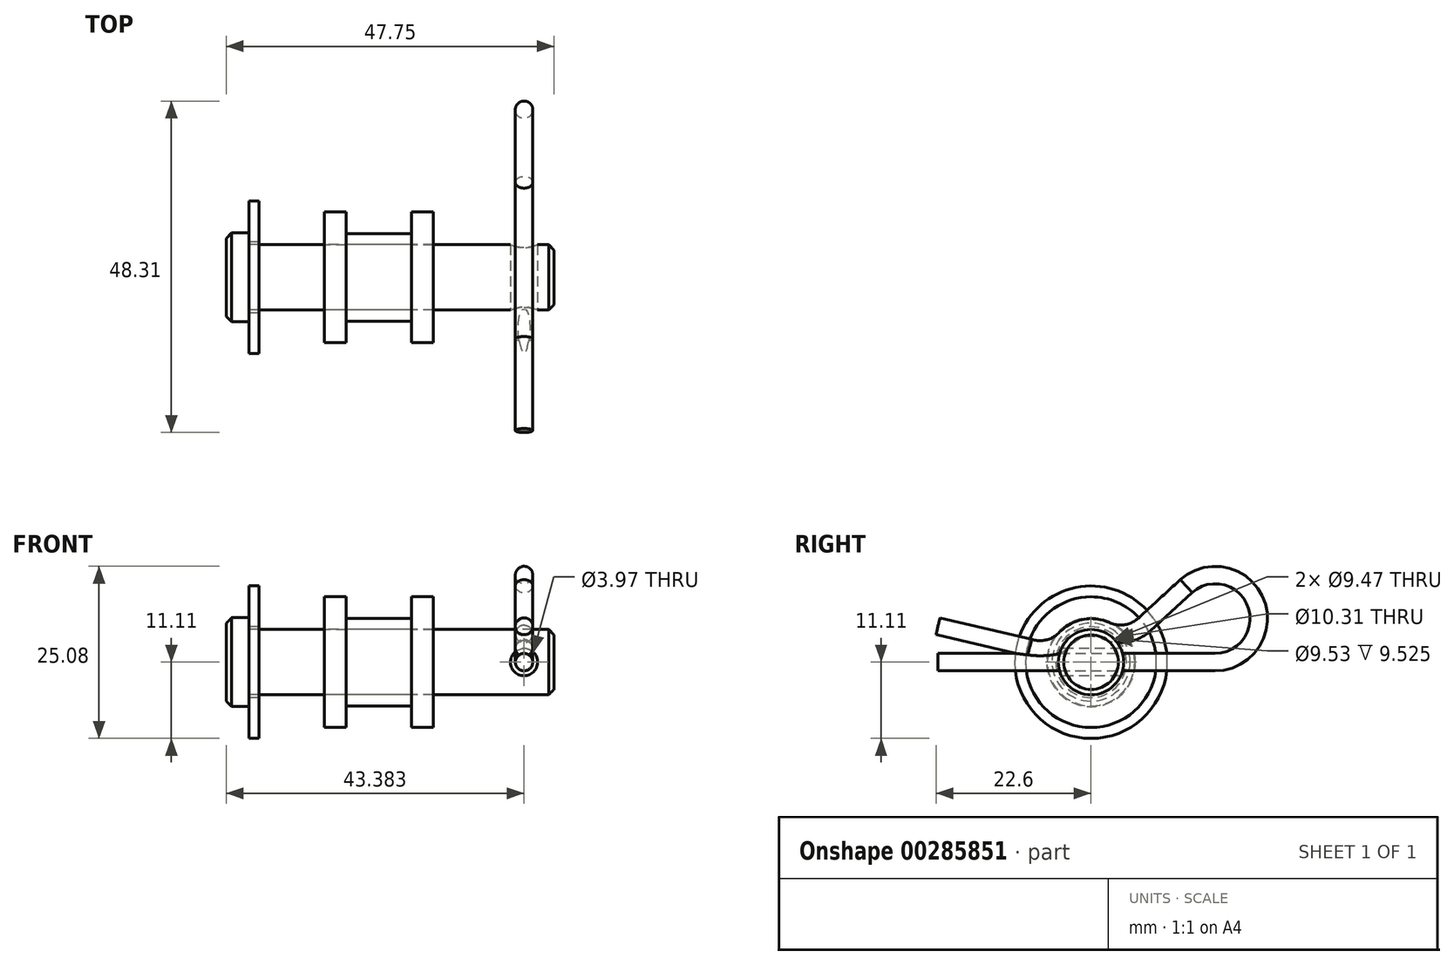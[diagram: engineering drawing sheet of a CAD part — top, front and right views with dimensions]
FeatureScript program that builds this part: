
annotation { "Feature Type Name" : "Feature", "Feature Type Description" : "" }
export const myFeature = defineFeature(function(context is Context, id is Id, definition is map)
    precondition{}
    {
        {
            var Q0;
            Q0=qCreatedBy(makeId("Front.planeOp"),FACE);
            var sketch = newSketch(context, id + "F0", { "sketchPlane" : qUnion([Q0])});
            skLineSegment(sketch, "E0", {"start": v(0, 0) * mm, "end": v(47.75, 0) * mm, "construction": true});
            skLineSegment(sketch, "E1", {"start": v(0, 0) * mm, "end": v(0, 6.48) * mm});
            skLineSegment(sketch, "E2", {"start": v(0, 6.48) * mm, "end": v(3.3, 6.48) * mm});
            skLineSegment(sketch, "E3", {"start": v(3.3, 6.48) * mm, "end": v(3.3, 4.76) * mm});
            skLineSegment(sketch, "E4", {"start": v(3.3, 4.76) * mm, "end": v(47.75, 4.76) * mm});
            skLineSegment(sketch, "E5", {"start": v(47.75, 4.76) * mm, "end": v(47.75, 0) * mm});
            skLineSegment(sketch, "E6", {"start": v(0, 0) * mm, "end": v(47.75, 0) * mm});
            skCircle(sketch, "E7", {"center": v(43.38, 0) * mm, "radius": 1.98 * mm});
            skSolve(sketch);
        }
        {
            var Q0;
            {var subQ0=sQuery(id+"F0.wireOp",EDGE,"E1");Q0=makeQuery(id+"F0.imprint","IMPRINT",FACE,{"disambiguationData":[TD([[makeQuery(id+"F0.imprint","IMPRINT",EDGE,{"derivedFrom":subQ0}),-1.0]])]});}
            var Q1;
            {var subQ0=sQuery(id+"F0.wireOp",EDGE,"E7");var subQ1=sQuery(id+"F0.wireOp",EDGE,"E6");var subQ2=makeQuery(id+"F0.imprint","INTERSECT",VERTEX,{"disambiguationData":[OD(0.0)],"derivedFrom":[subQ1,subQ0]});Q1=makeQuery(id+"F0.imprint","IMPRINT",FACE,{"disambiguationData":[TD([[makeQuery(id+"F0.imprint","IMPRINT",EDGE,{"disambiguationData":[TD([[subQ2,-1.0]])],"derivedFrom":subQ1}),1.0]])]});}
            var Q2;
            Q2=sQuery(id+"F0.wireOp",EDGE,"E6");
            revolve(context, id + "F1", {"entities" : qUnion([Q0, Q1]), "axis" : qUnion([Q2]), "revolveType" : RevolveType.FULL});
        }
        {
            var Q0;
            {var subQ0=sQuery(id+"F0.wireOp",EDGE,"E7");var subQ1=sQuery(id+"F0.wireOp",EDGE,"E6");var subQ2=makeQuery(id+"F0.imprint","INTERSECT",VERTEX,{"disambiguationData":[OD(0.0)],"derivedFrom":[subQ1,subQ0]});Q0=makeQuery(id+"F0.imprint","IMPRINT",FACE,{"disambiguationData":[TD([[makeQuery(id+"F0.imprint","IMPRINT",EDGE,{"disambiguationData":[TD([[subQ2,-1.0]])],"derivedFrom":subQ1}),-1.0]])]});}
            var Q1;
            {var subQ0=sQuery(id+"F0.wireOp",EDGE,"E7");var subQ1=sQuery(id+"F0.wireOp",EDGE,"E6");var subQ2=makeQuery(id+"F0.imprint","INTERSECT",VERTEX,{"disambiguationData":[OD(0.0)],"derivedFrom":[subQ1,subQ0]});Q1=makeQuery(id+"F0.imprint","IMPRINT",FACE,{"disambiguationData":[TD([[makeQuery(id+"F0.imprint","IMPRINT",EDGE,{"disambiguationData":[TD([[subQ2,-1.0]])],"derivedFrom":subQ1}),1.0]])]});}
            extrude(context, id + "F2", {"entities" : qUnion([Q0, Q1]), "operationType" : NewBodyOperationType.REMOVE, "endBound" : BoundingType.THROUGH_ALL, "oppositeDirection" : true, "depth" : 25.4 * mm, "hasSecondDirection" : true, "secondDirectionBound" : SecondDirectionBoundingType.THROUGH_ALL, "secondDirectionOppositeDirection" : false, "secondDirectionDepth" : 25.4 * mm});
        }
        {
            var Q0;
            Q0=makeQuery(id+"F1.opRevolve","SWEPT_FACE",FACE,{"disambiguationData":[OSD([sQuery(id+"F0.wireOp",EDGE,"E3")])]});
            var sketch = newSketch(context, id + "F3", { "sketchPlane" : qUnion([Q0])});
            skCircle(sketch, "E8", {"center": v(0, 0) * mm, "radius": 5.16 * mm});
            skCircle(sketch, "E9", {"center": v(0, 0) * mm, "radius": 11.11 * mm});
            skSolve(sketch);
        }
        {
            var Q0;
            Q0 = qSketchRegion(id + "F3", true);
            extrude(context, id + "F4", {"entities" : qUnion([Q0]), "depth" : 1.45 * mm});
        }
        {
            var Q0;
            Q0=makeQuery(id+"F1.opRevolve","SWEPT_EDGE",EDGE,{"disambiguationData":[OSD([sQuery(id+"F0.wireOp",EDGE,"E4"),sQuery(id+"F0.wireOp",EDGE,"E5")])]});
            var Q1;
            Q1=makeQuery(id+"F1.opRevolve","SWEPT_EDGE",EDGE,{"disambiguationData":[OSD([sQuery(id+"F0.wireOp",EDGE,"E1"),sQuery(id+"F0.wireOp",EDGE,"E2")])]});
            chamfer(context, id + "F5", {"entities" : qUnion([Q0, Q1]), "width" : 0.79 * mm, "tangentPropagation" : true});
        }
        {
            var Q0;
            Q0=qCreatedBy(makeId("Front.planeOp"),FACE);
            var sketch = newSketch(context, id + "F6", { "sketchPlane" : qUnion([Q0])});
            skLineSegment(sketch, "E10", {"start": v(14.3, 4.74) * mm, "end": v(14.3, 9.53) * mm});
            skLineSegment(sketch, "E11", {"start": v(14.3, 9.53) * mm, "end": v(17.48, 9.53) * mm});
            skLineSegment(sketch, "E12", {"start": v(17.48, 9.53) * mm, "end": v(17.48, 4.74) * mm});
            skLineSegment(sketch, "E13", {"start": v(14.3, 4.74) * mm, "end": v(17.48, 4.74) * mm});
            skLineSegment(sketch, "E14.bottom", {"start": v(17.48, 6.38) * mm, "end": v(27, 6.38) * mm});
            skLineSegment(sketch, "E14.top", {"start": v(17.48, 4.76) * mm, "end": v(27, 4.76) * mm});
            skLineSegment(sketch, "E14.left", {"start": v(17.48, 6.38) * mm, "end": v(17.48, 4.76) * mm});
            skLineSegment(sketch, "E14.right", {"start": v(27, 6.38) * mm, "end": v(27, 4.76) * mm});
            skLineSegment(sketch, "E15", {"start": v(22.24, 6.38) * mm, "end": v(22.24, 4.76) * mm, "construction": true});
            skLineSegment(sketch, "E16.MirrorCS", {"start": v(30.18, 4.74) * mm, "end": v(30.18, 9.53) * mm});
            skLineSegment(sketch, "E17.MirrorCS", {"start": v(30.18, 9.53) * mm, "end": v(27, 9.53) * mm});
            skLineSegment(sketch, "E18.MirrorCS", {"start": v(27, 9.53) * mm, "end": v(27, 4.74) * mm});
            skLineSegment(sketch, "E19.MirrorCS", {"start": v(30.18, 4.74) * mm, "end": v(27, 4.74) * mm});
            skSolve(sketch);
        }
        {
            var Q0;
            Q0=makeQuery(id+"F6.imprint","IMPRINT",FACE,{"disambiguationData":[TD([[makeQuery(id+"F6.imprint","IMPRINT",EDGE,{"derivedFrom":sQuery(id+"F6.wireOp",EDGE,"E10")}),-1.0]])]});
            var Q1;
            Q1=sQuery(id+"F0.wireOp",EDGE,"E6");
            revolve(context, id + "F7", {"entities" : qUnion([Q0]), "axis" : qUnion([Q1]), "revolveType" : RevolveType.FULL});
        }
        {
            var Q0;
            {var subQ0=sQuery(id+"F6.wireOp",EDGE,"E14.bottom");Q0=makeQuery(id+"F6.imprint","IMPRINT",FACE,{"disambiguationData":[TD([[makeQuery(id+"F6.imprint","IMPRINT",EDGE,{"derivedFrom":subQ0}),-1.0]])]});}
            var Q1;
            Q1=sQuery(id+"F0.wireOp",EDGE,"E6");
            revolve(context, id + "F8", {"entities" : qUnion([Q0]), "axis" : qUnion([Q1]), "revolveType" : RevolveType.FULL});
        }
        {
            var Q0;
            Q0=makeQuery(id+"F6.imprint","IMPRINT",FACE,{"disambiguationData":[TD([[makeQuery(id+"F6.imprint","IMPRINT",EDGE,{"derivedFrom":sQuery(id+"F6.wireOp",EDGE,"E16.MirrorCS")}),1.0]])]});
            var Q1;
            Q1=sQuery(id+"F0.wireOp",EDGE,"E6");
            revolve(context, id + "F9", {"entities" : qUnion([Q0]), "axis" : qUnion([Q1]), "revolveType" : RevolveType.FULL});
        }
        {
            var Q0;
            Q0=makeQuery(id+"F1.opRevolve","SWEPT_FACE",FACE,{"disambiguationData":[OSD([sQuery(id+"F0.wireOp",EDGE,"E5")])]});
            cPlane(context, id + "F10", {"entities" : qUnion([Q0]), "cplaneType" : CPlaneType.OFFSET, "offset" : 4.37 * mm, "oppositeDirection" : true, "width" : 152.4 * mm, "height" : 152.4 * mm});
        }
        {
            var Q0;
            Q0=qCreatedBy(id+"F10.planeOp",FACE);
            var sketch = newSketch(context, id + "F11", { "sketchPlane" : qUnion([Q0])});
            skLineSegment(sketch, "E20", {"start": v(-22.32, 0) * mm, "end": v(18.09, 0) * mm});
            skArc(sketch, "E21", {"start": v(18.09, 0) * mm, "mid": v(24.02, 8.61) * mm, "end": v(13.86, 11.09) * mm});
            skLineSegment(sketch, "E22", {"start": v(-22.32, 5.23) * mm, "end": v(-8.78, 2.05) * mm});
            skArc(sketch, "E23", {"start": v(-8.78, 2.05) * mm, "mid": v(-6.04, 2.06) * mm, "end": v(-3.7, 3.47) * mm});
            skArc(sketch, "E24", {"start": v(2.15, 4.6) * mm, "mid": v(5.07, 4.19) * mm, "end": v(7.73, 5.46) * mm});
            skLineSegment(sketch, "E25", {"start": v(13.86, 11.09) * mm, "end": v(7.73, 5.46) * mm});
            skArc(sketch, "E26.trimOffspring", {"start": v(2.15, 4.6) * mm, "mid": v(-0.96, 4.98) * mm, "end": v(-3.7, 3.47) * mm});
            skSolve(sketch);
        }
        {
            var Q0;
            Q0=qCreatedBy(makeId("Front.planeOp"),FACE);
            cPlane(context, id + "F12", {"entities" : qUnion([Q0]), "cplaneType" : CPlaneType.OFFSET, "offset" : 22.33 * mm, "width" : 152.4 * mm, "height" : 152.4 * mm});
        }
        {
            var Q0;
            Q0=qCreatedBy(id+"F12.planeOp",FACE);
            var sketch = newSketch(context, id + "F13", { "sketchPlane" : qUnion([Q0])});
            skCircle(sketch, "E27", {"center": v(43.38, 0) * mm, "radius": 1.27 * mm});
            skSolve(sketch);
        }
        {
            var Q0;
            Q0 = qSketchRegion(id + "F13", true);
            var Q1;
            Q1 = qConstructionFilter(qBodyType(qCreatedBy(id + "F11" ,EDGE), BodyType.WIRE), ConstructionObject.NO);
            sweep(context, id + "F14", {"profiles" : qUnion([Q0]), "path" : qUnion([Q1])});
        }
    });
